# Revit family: Haworth_Immerse_SingleTable_Square
name_source: partatom
category: Furniture Systems
revit_build: Autodesk Revit 2018 (Build: 20170223_1515(x64)
units: mm (PartAtom-declared; Revit-internal decimal feet)

## family parameters
Always vertical = Yes
Cut with Voids When Loaded = No
OmniClass Number = 23.40.70.14.64.21
OmniClass Title = Systems Furniture
Part Type = Normal
Room Calculation Point = No
Round Connector Dimension = Use Diameter
Shared = No
Work Plane-Based = No

## types (6) — shared parameters
Assembly Code = E2020200
Edge Offset = 2"
Manufacturer = Haworth
Note = Planter only available on 60"w option
Revision Number = 1
Size = Verify Final Dim w/ Haworth
Standard Diameter = 48, 60 in.
Standard Height = 29, 36, 39 in.
URL = https://www.haworth.com
URL - Product = http://www.haworth.com
Understructure Inset = 15 177/256"
Understucture Thickness = 1 69/128"
Void Baseline Height = 18"
Void Diameter = 17 169/256"
Warranty = http://www.haworth.com

## per-type parameters (varying)
| type | 29 in. Height | 36 in. Height | 39 in. Height | Actual Depth | Actual Height | Blend Bottom Diameter | Description | Large | Model | Round Planter | Round Planter Actual | Round Planter Void Height | Small | Understructure Width | Understuctuer Bottom |
| 48w 29h - No Planter | Yes | No | No | 48" | 29" | 44" | Haworth Immerse Single Table Square - 48w 29h - No Planter | No | THRQ-4848 | No | No | 6" | Yes | 16 79/128" | 26 29/64" |
| 48w 36h - No Planter | No | Yes | No | 48" | 36" | 44" | Haworth Immerse Single Table Square - 48w 36h - No Planter | No | THRQ-4848 | No | No | 6" | Yes | 16 79/128" | 33 29/64" |
| 48w 39h - No Planter | No | No | Yes | 48" | 39" | 44" | Haworth Immerse Single Table Square - 48w 39h - No Planter | No | THRQ-4848 | No | No | 6" | Yes | 16 79/128" | 36 29/64" |
| 60w 29h - Round Planter | Yes | No | No | 60" | 29" | 56" | Haworth Immerse Single Table Square - 60w 29h - Round Planter | Yes | THRQ-6060 | Yes | Yes | 24" | No | 28 79/128" | 26 29/64" |
| 60w 36h - Round Planter | No | Yes | No | 60" | 36" | 56" | Haworth Immerse Single Table Square - 60w 36h - Round Planter | Yes | THRQ-6060 | Yes | Yes | 24" | No | 28 79/128" | 33 29/64" |
| 60w 39h - Round Planter | No | No | Yes | 60" | 39" | 56" | Haworth Immerse Single Table Square - 60w 39h - Round Planter | Yes | THRQ-6060 | Yes | Yes | 24" | No | 28 79/128" | 36 29/64" |

## geometry (parser evidence)
native form markers: Blend x1, Sweep x6
no freeform markers — native parametric forms only
